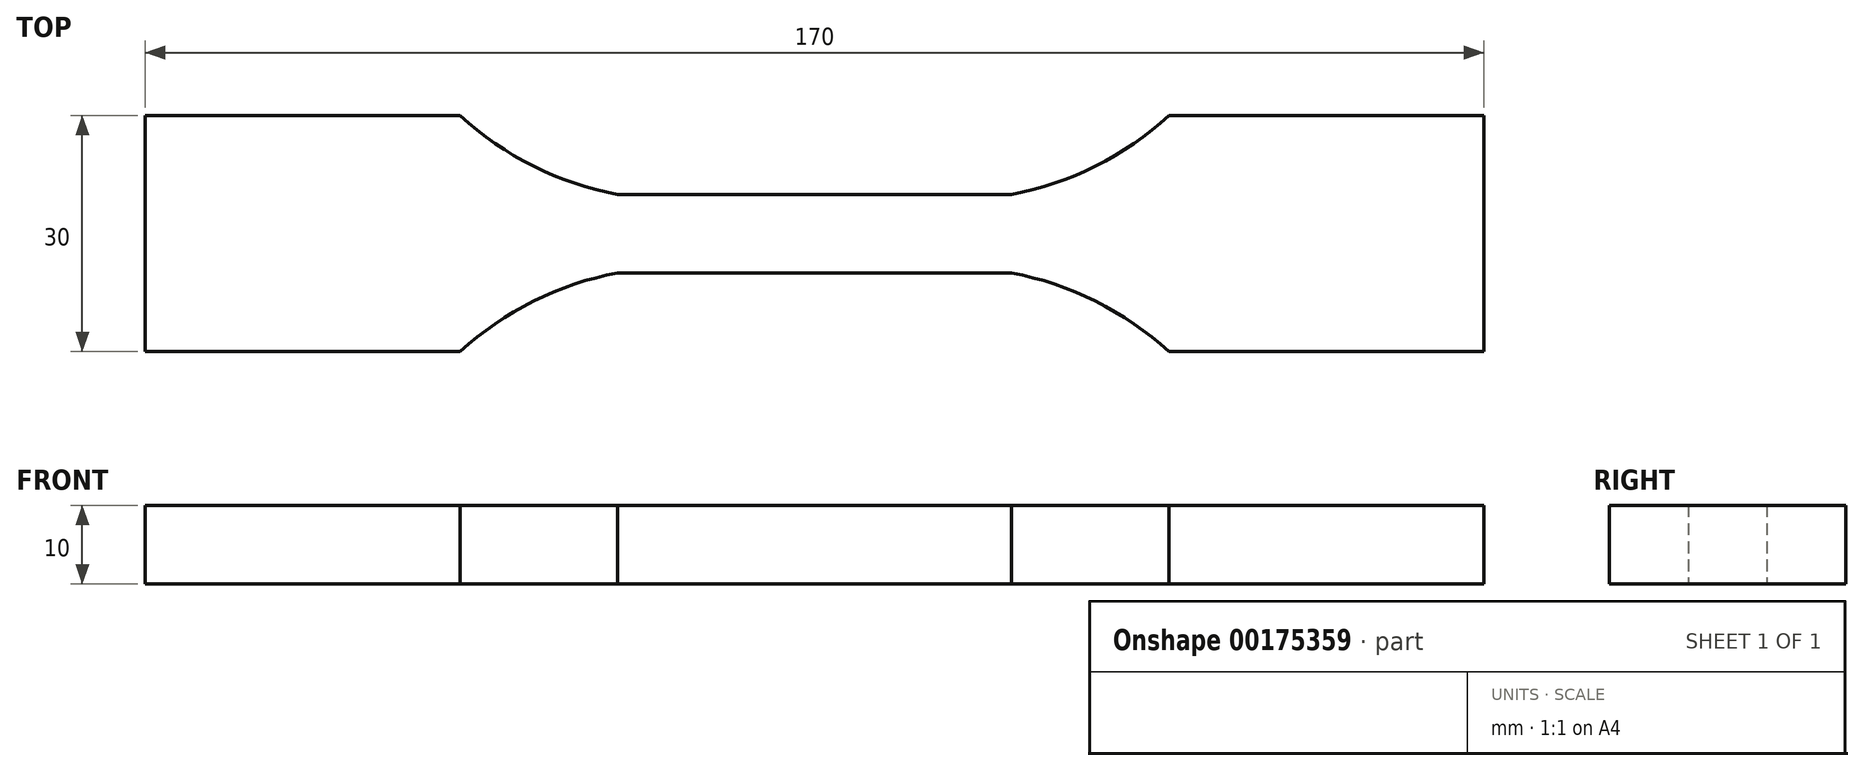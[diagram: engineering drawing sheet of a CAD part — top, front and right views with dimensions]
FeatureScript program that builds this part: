
annotation { "Feature Type Name" : "Feature", "Feature Type Description" : "" }
export const myFeature = defineFeature(function(context is Context, id is Id, definition is map)
    precondition{}
    {
        {
            var Q0;
            Q0=qCreatedBy(makeId("Top.planeOp"),FACE);
            var sketch = newSketch(context, id + "F0", { "sketchPlane" : qUnion([Q0])});
            skLineSegment(sketch, "E0.bottom", {"start": v(15, -85) * mm, "end": v(-15, -85) * mm});
            skLineSegment(sketch, "E0.top", {"start": v(15, 85) * mm, "end": v(-15, 85) * mm});
            skLineSegment(sketch, "E0.left", {"start": v(15, -85) * mm, "end": v(15, -45) * mm});
            skLineSegment(sketch, "E0.right", {"start": v(-15, -85) * mm, "end": v(-15, -45) * mm});
            skPoint(sketch, "E0.middle", {"position": v(0, 0) * mm});
            skPoint(sketch, "E1", {"position": v(5, 25) * mm});
            skPoint(sketch, "E2", {"position": v(-5, 25) * mm});
            skArc(sketch, "E3", {"start": v(15, 45) * mm, "mid": v(8.57, 35.71) * mm, "end": v(5, 25) * mm});
            skArc(sketch, "E4", {"start": v(-5, 25) * mm, "mid": v(-8.57, 35.71) * mm, "end": v(-15, 45) * mm});
            skPoint(sketch, "E5", {"position": v(5, -25) * mm});
            skPoint(sketch, "E6", {"position": v(-5, -25) * mm});
            skArc(sketch, "E7", {"start": v(5, -25) * mm, "mid": v(8.57, -35.71) * mm, "end": v(15, -45) * mm});
            skArc(sketch, "E8", {"start": v(-15, -45) * mm, "mid": v(-8.57, -35.71) * mm, "end": v(-5, -25) * mm});
            skLineSegment(sketch, "E9.trimOffspring", {"start": v(15, 45) * mm, "end": v(15, 85) * mm});
            skLineSegment(sketch, "E10.trimOffspring", {"start": v(-15, 45) * mm, "end": v(-15, 85) * mm});
            skLineSegment(sketch, "E11.trimOffspring", {"start": v(-5, 25) * mm, "end": v(-5, -25) * mm});
            skLineSegment(sketch, "E12.trimOffspring", {"start": v(5, 25) * mm, "end": v(5, -25) * mm});
            skSolve(sketch);
        }
        {
            var Q0;
            Q0 = qSketchRegion(id + "F0", true);
            extrude(context, id + "F1", {"entities" : qUnion([Q0]), "depth" : 10 * mm});
        }
        {
            var Q0;
            Q0=makeQuery(id+"F1.opExtrude","SWEPT_BODY",BODY,{"disambiguationData":[OSD([sQuery(id+"F0.wireOp",EDGE,"E0.bottom"),sQuery(id+"F0.wireOp",EDGE,"E0.top"),sQuery(id+"F0.wireOp",EDGE,"E0.left"),sQuery(id+"F0.wireOp",EDGE,"E0.right"),sQuery(id+"F0.wireOp",EDGE,"E3"),sQuery(id+"F0.wireOp",EDGE,"E4"),sQuery(id+"F0.wireOp",EDGE,"E7"),sQuery(id+"F0.wireOp",EDGE,"E8"),sQuery(id+"F0.wireOp",EDGE,"E9.trimOffspring"),sQuery(id+"F0.wireOp",EDGE,"E10.trimOffspring"),sQuery(id+"F0.wireOp",EDGE,"E11.trimOffspring"),sQuery(id+"F0.wireOp",EDGE,"E12.trimOffspring")])]});
            var Q1;
            Q1=makeQuery(id+"F1.opExtrude","SWEPT_EDGE",EDGE,{"disambiguationData":[OSD([sQuery(id+"F0.wireOp",EDGE,"E0.bottom"),sQuery(id+"F0.wireOp",EDGE,"E0.right")])]});
            transform(context, id + "F2", {"entities" : qUnion([Q0]), "transformType" : TransformType.ROTATION, "transformAxis" : qUnion([Q1]), "angle" : 90 * degree, "makeCopy" : false});
        }
        {
            var Q0;
            Q0=makeQuery(id+"F1.opExtrude","SWEPT_BODY",BODY,{"disambiguationData":[OSD([sQuery(id+"F0.wireOp",EDGE,"E0.bottom"),sQuery(id+"F0.wireOp",EDGE,"E0.top"),sQuery(id+"F0.wireOp",EDGE,"E0.left"),sQuery(id+"F0.wireOp",EDGE,"E0.right"),sQuery(id+"F0.wireOp",EDGE,"E3"),sQuery(id+"F0.wireOp",EDGE,"E4"),sQuery(id+"F0.wireOp",EDGE,"E7"),sQuery(id+"F0.wireOp",EDGE,"E8"),sQuery(id+"F0.wireOp",EDGE,"E9.trimOffspring"),sQuery(id+"F0.wireOp",EDGE,"E10.trimOffspring"),sQuery(id+"F0.wireOp",EDGE,"E11.trimOffspring"),sQuery(id+"F0.wireOp",EDGE,"E12.trimOffspring")])]});
            transform(context, id + "F3", {"entities" : qUnion([Q0]), "transformType" : TransformType.TRANSLATION_3D, "dx" : -70 * mm, "dy" : 100 * mm, "dz" : 0 * mm, "makeCopy" : false});
        }
        {
            var Q0;
            Q0=makeQuery(id+"F1.opExtrude","SWEPT_BODY",BODY,{"disambiguationData":[OSD([sQuery(id+"F0.wireOp",EDGE,"E0.bottom"),sQuery(id+"F0.wireOp",EDGE,"E0.top"),sQuery(id+"F0.wireOp",EDGE,"E0.left"),sQuery(id+"F0.wireOp",EDGE,"E0.right"),sQuery(id+"F0.wireOp",EDGE,"E3"),sQuery(id+"F0.wireOp",EDGE,"E4"),sQuery(id+"F0.wireOp",EDGE,"E7"),sQuery(id+"F0.wireOp",EDGE,"E8"),sQuery(id+"F0.wireOp",EDGE,"E9.trimOffspring"),sQuery(id+"F0.wireOp",EDGE,"E10.trimOffspring"),sQuery(id+"F0.wireOp",EDGE,"E11.trimOffspring"),sQuery(id+"F0.wireOp",EDGE,"E12.trimOffspring")])]});
            transform(context, id + "F4", {"entities" : qUnion([Q0]), "transformType" : TransformType.TRANSLATION_3D, "dx" : -200 * mm, "dy" : 0 * mm, "dz" : 0 * mm, "makeCopy" : false});
        }
    });
